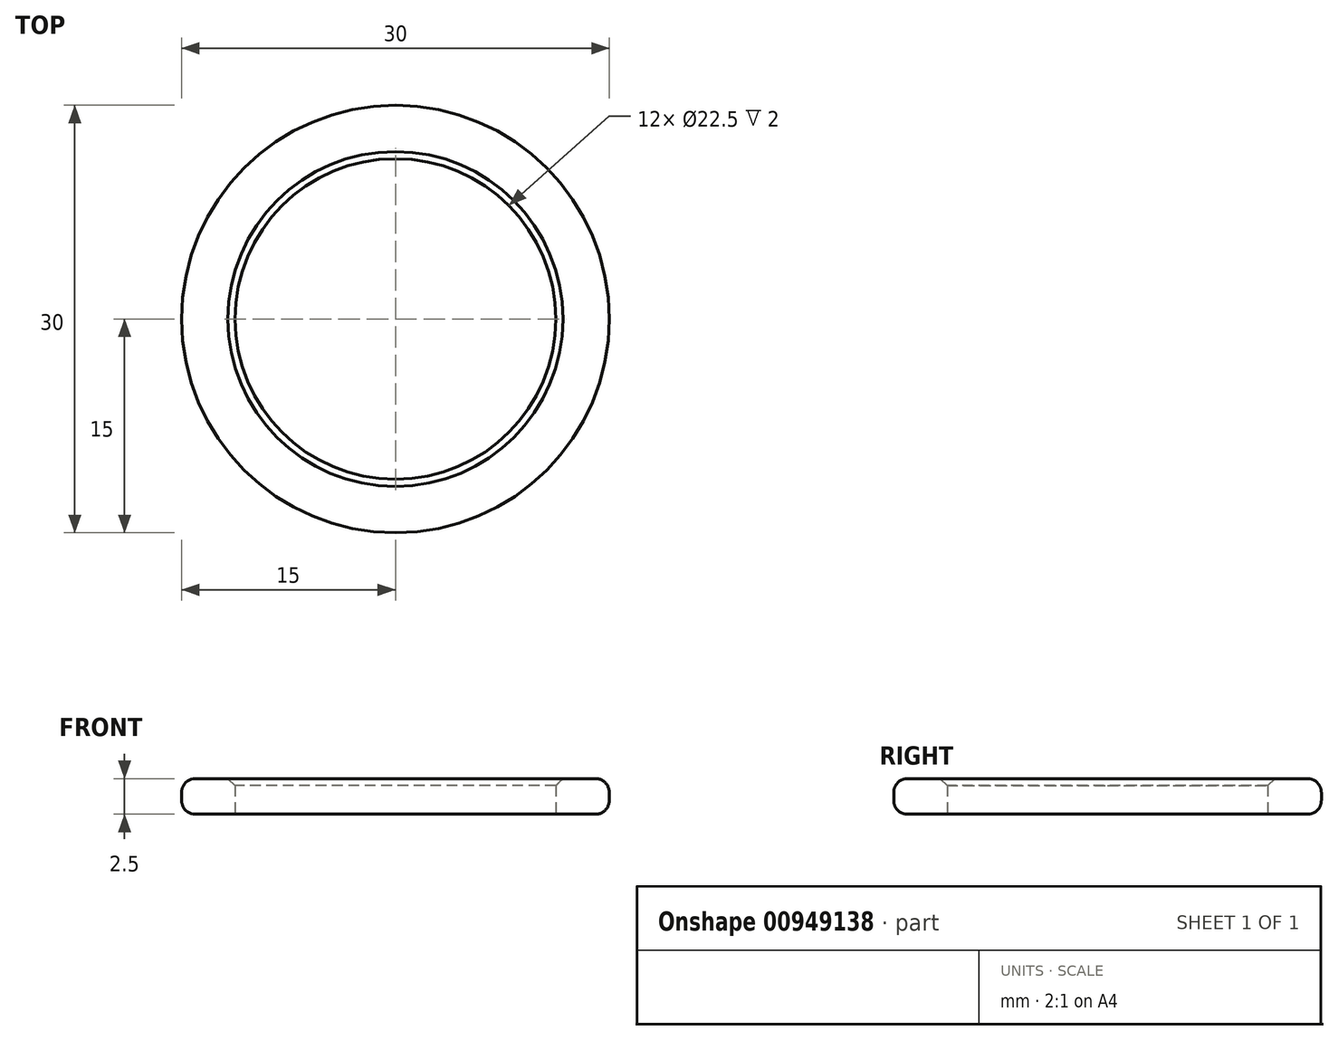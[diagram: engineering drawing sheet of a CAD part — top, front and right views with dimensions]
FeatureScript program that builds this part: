
annotation { "Feature Type Name" : "Feature", "Feature Type Description" : "" }
export const myFeature = defineFeature(function(context is Context, id is Id, definition is map)
    precondition{}
    {
        {
            var Q0;
            Q0=qCreatedBy(makeId("Top.planeOp"),FACE);
            var sketch = newSketch(context, id + "F0", { "sketchPlane" : qUnion([Q0])});
            skCircle(sketch, "E0", {"center": v(0, 0) * mm, "radius": 15 * mm});
            skCircle(sketch, "E1", {"center": v(0, 0) * mm, "radius": 11.25 * mm});
            skSolve(sketch);
        }
        {
            var Q0;
            Q0=makeQuery(id+"F0.imprint","IMPRINT",FACE,{"disambiguationData":[TD([[makeQuery(id+"F0.imprint","IMPRINT",EDGE,{"derivedFrom":sQuery(id+"F0.wireOp",EDGE,"E0")}),1.0]])]});
            extrude(context, id + "F1", {"entities" : qUnion([Q0]), "depth" : 2.5 * mm, "offsetDistance" : 25 * mm});
        }
        {
            var Q0;
            Q0=makeQuery(id+"F1.opExtrude","CAP_EDGE",EDGE,{"disambiguationData":[OSD([sQuery(id+"F0.wireOp",EDGE,"E1")])],"isStart":false});
            chamfer(context, id + "F2", {"entities" : qUnion([Q0]), "width" : .5 * mm, "tangentPropagation" : true});
        }
        {
            var Q0;
            Q0=makeQuery(id+"F1.opExtrude","CAP_EDGE",EDGE,{"disambiguationData":[OSD([sQuery(id+"F0.wireOp",EDGE,"E0")])],"isStart":false});
            var Q1;
            Q1=makeQuery(id+"F1.opExtrude","CAP_EDGE",EDGE,{"disambiguationData":[OSD([sQuery(id+"F0.wireOp",EDGE,"E0")])],"isStart":true});
            fillet(context, id + "F3", {"entities" : qUnion([Q0, Q1]), "radius" : 0.96 * mm, "tangentPropagation" : true, "allowEdgeOverflow" : false});
        }
    });
